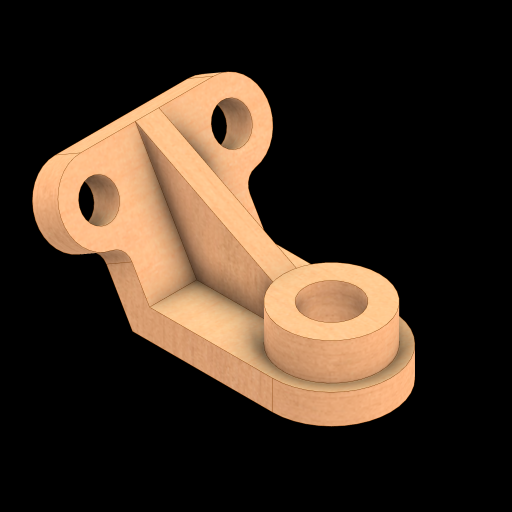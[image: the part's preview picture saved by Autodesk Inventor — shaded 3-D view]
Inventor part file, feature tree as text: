
AUTODESK INVENTOR PART (.ipt)
format: ipt  version: 2024 (Build 280153000, 153)  size: 340,992 bytes
history: native  units: mm
features: extrude x5, sketch x5, fillet x1, hole x1, other x1, projected_geometry x1
ambient origin geometry x8: Origin, YZ Plane, XZ Plane, XY Plane, X Axis, Y Axis, Z Axis, Center Point
bodies: Solid1 (feature_tree)
feature tree (14):
  extrude  "BASE"  Depth=95.0mm
  extrude  "EARS"  TaperAngle=120.0deg  [1 undecoded]
  fillet  "Fillet1"  Radius=20.0mm
  hole  "EARHOLES"  [1 undecoded]
  sketch  "Sketch4"  dims[d10=45.0mm d11=50.0mm]
  extrude  "ROUNDED END"  Depth=45.0mm
  extrude  "RAISED BOSS"  Depth=10.0mm
  extrude  "BOSS CUTOUT"  Depth=16.0mm
  other  "CONNECTING RIB"
  sketch  "Sketch1"  dims[d0=95.0mm d1=95.0mm]
  sketch  "Sketch2"  dims[d2=20.0mm d5=120.0deg d6=20.0mm]
  sketch  "Sketch3"  dims[d7=80.0mm d8=0.0mm d9=90.0mm]
  sketch  "Sketch5"  dims[d12=20.0mm d13=0.0mm d14=10.0mm d15=25.0mm d16=6.0mm d17=4.0mm d18=2.0mm d19=90.0deg d20=8.0mm d21=20.594885mm d22=35.0mm d23=65.0mm d24=20.0mm d25=0.0mm d26=25.0mm d27=0.0mm d28=0.0mm d29=0.0mm d30=1.0mm d31=16.0mm d32=0.0mm d33=0.0mm d34=1.0mm d35=1.0mm]
  projected_geometry  "Projected Loop1"
note: 2 required parameter values undecoded (feature->parameter linkage not recoverable at this tier; creation-order binding heuristic only, values carry confidence <= 0.55)
